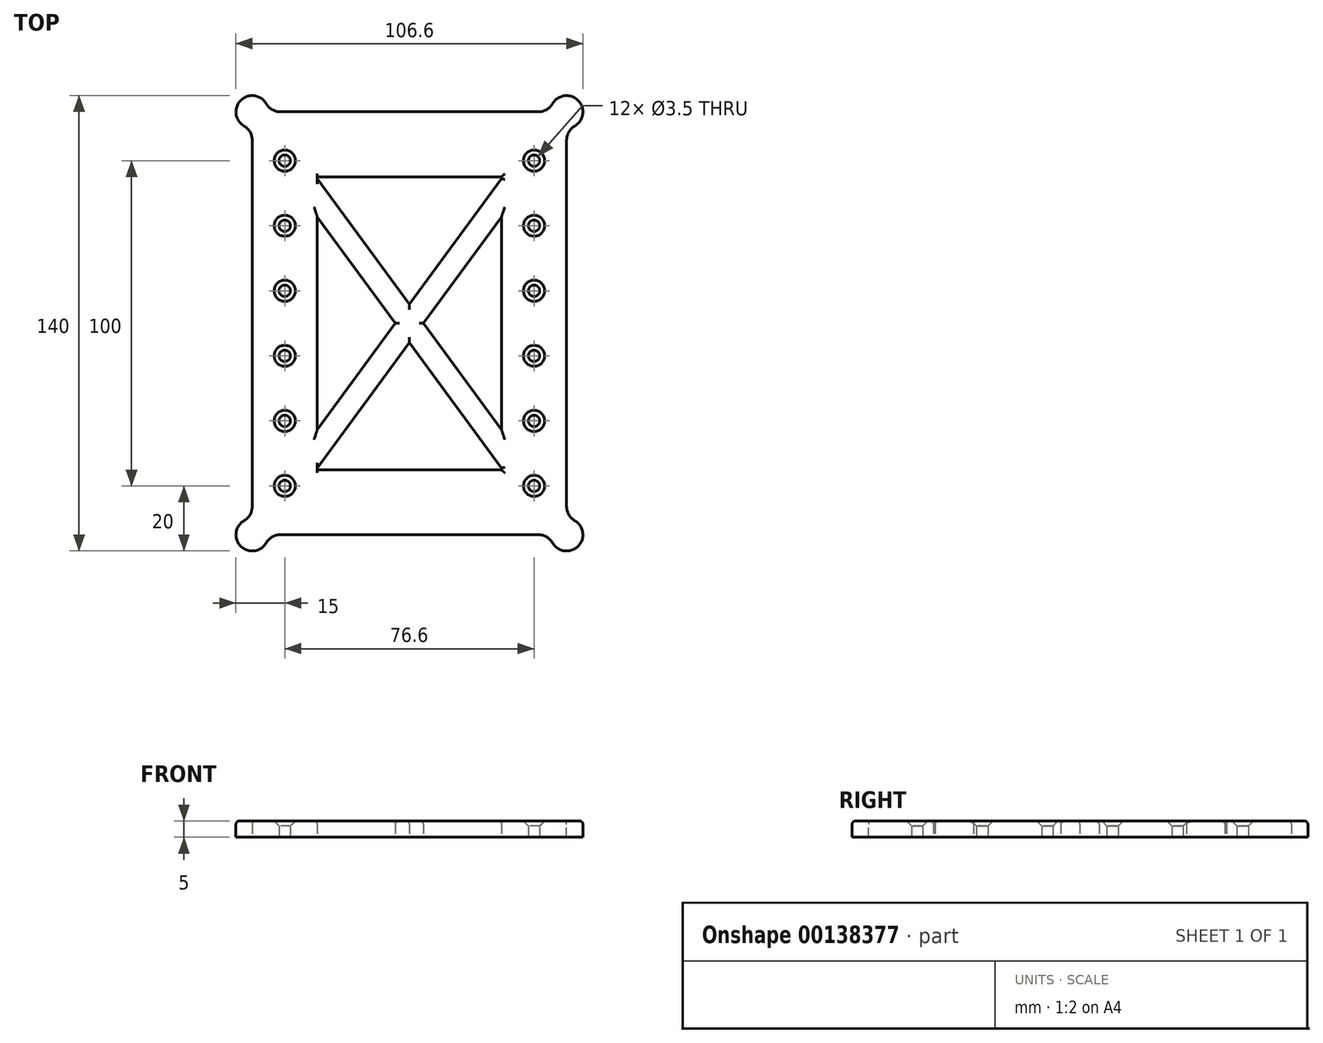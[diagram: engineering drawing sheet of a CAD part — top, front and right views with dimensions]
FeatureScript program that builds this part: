
annotation { "Feature Type Name" : "Feature", "Feature Type Description" : "" }
export const myFeature = defineFeature(function(context is Context, id is Id, definition is map)
    precondition{}
    {
        {
            var Q0;
            Q0=qCreatedBy(makeId("Top.planeOp"),FACE);
            var sketch = newSketch(context, id + "F0", { "sketchPlane" : qUnion([Q0])});
            skLineSegment(sketch, "E0.bottom", {"start": v(5, 0) * mm, "end": v(91.6, 0) * mm});
            skLineSegment(sketch, "E0.top", {"start": v(5, 130) * mm, "end": v(91.6, 130) * mm});
            skLineSegment(sketch, "E0.left", {"start": v(0, 5) * mm, "end": v(0, 125) * mm});
            skLineSegment(sketch, "E0.right", {"start": v(96.6, 5) * mm, "end": v(96.6, 125) * mm});
            skCircle(sketch, "E1", {"center": v(10, 15) * mm, "radius": 1.75 * mm});
            skCircle(sketch, "E2.0.1.0", {"center": v(10, 35) * mm, "radius": 1.75 * mm});
            skCircle(sketch, "E2.0.2.0", {"center": v(10, 55) * mm, "radius": 1.75 * mm});
            skCircle(sketch, "E2.0.3.0", {"center": v(10, 75) * mm, "radius": 1.75 * mm});
            skCircle(sketch, "E2.0.4.0", {"center": v(10, 95) * mm, "radius": 1.75 * mm});
            skCircle(sketch, "E2.0.5.0", {"center": v(10, 115) * mm, "radius": 1.75 * mm});
            skCircle(sketch, "E2.1.0.0", {"center": v(86.6, 15) * mm, "radius": 1.75 * mm});
            skCircle(sketch, "E2.1.1.0", {"center": v(86.6, 35) * mm, "radius": 1.75 * mm});
            skCircle(sketch, "E2.1.2.0", {"center": v(86.6, 55) * mm, "radius": 1.75 * mm});
            skCircle(sketch, "E2.1.3.0", {"center": v(86.6, 75) * mm, "radius": 1.75 * mm});
            skCircle(sketch, "E2.1.4.0", {"center": v(86.6, 95) * mm, "radius": 1.75 * mm});
            skCircle(sketch, "E2.1.5.0", {"center": v(86.6, 115) * mm, "radius": 1.75 * mm});
            skLineSegment(sketch, "E2.direction1", {"start": v(10, 15) * mm, "end": v(86.6, 15) * mm, "construction": true});
            skLineSegment(sketch, "E2.direction2", {"start": v(10, 15) * mm, "end": v(10, 35) * mm, "construction": true});
            skArc(sketch, "E3", {"start": v(0, 5) * mm, "mid": v(-3.54, -3.54) * mm, "end": v(5, 0) * mm});
            skArc(sketch, "E4", {"start": v(91.6, 0) * mm, "mid": v(100.14, -3.54) * mm, "end": v(96.6, 5) * mm});
            skArc(sketch, "E5", {"start": v(96.6, 125) * mm, "mid": v(100.14, 133.54) * mm, "end": v(91.6, 130) * mm});
            skArc(sketch, "E6", {"start": v(5, 130) * mm, "mid": v(-3.54, 133.54) * mm, "end": v(0, 125) * mm});
            skLineSegment(sketch, "E7.0", {"start": v(20, 20) * mm, "end": v(20, 20.47) * mm});
            skLineSegment(sketch, "E7.2", {"start": v(76.6, 20) * mm, "end": v(76.6, 20.47) * mm});
            skLineSegment(sketch, "E7.3", {"start": v(20, 110) * mm, "end": v(45.8, 110) * mm});
            skLineSegment(sketch, "E8.trimOffspring", {"start": v(76.6, 67.5) * mm, "end": v(76.6, 97.7) * mm});
            skLineSegment(sketch, "E9.trimOffspring", {"start": v(20, 67.5) * mm, "end": v(20, 97.7) * mm});
            skLineSegment(sketch, "E10.trimOffspring", {"start": v(50.8, 110) * mm, "end": v(76.6, 110) * mm});
            skLineSegment(sketch, "E11", {"start": v(20, 97.7) * mm, "end": v(42.14, 67.5) * mm});
            skLineSegment(sketch, "E12", {"start": v(76.6, 32.3) * mm, "end": v(54.46, 62.5) * mm});
            skLineSegment(sketch, "E13", {"start": v(76.6, 109.53) * mm, "end": v(50.8, 74.32) * mm});
            skLineSegment(sketch, "E14", {"start": v(20, 20.47) * mm, "end": v(45.8, 55.68) * mm});
            skLineSegment(sketch, "E15.trimOffspring", {"start": v(20, 109.53) * mm, "end": v(20, 110) * mm});
            skLineSegment(sketch, "E16.trimOffspring", {"start": v(20, 32.3) * mm, "end": v(20, 62.5) * mm});
            skLineSegment(sketch, "E17.trimOffspring", {"start": v(76.6, 32.3) * mm, "end": v(76.6, 62.5) * mm});
            skLineSegment(sketch, "E18.trimOffspring", {"start": v(76.6, 109.53) * mm, "end": v(76.6, 110) * mm});
            skLineSegment(sketch, "E19.trimOffspring", {"start": v(42.14, 62.5) * mm, "end": v(20, 32.3) * mm});
            skLineSegment(sketch, "E20.trimOffspring", {"start": v(45.8, 74.32) * mm, "end": v(20, 109.53) * mm});
            skLineSegment(sketch, "E21.trimOffspring", {"start": v(54.46, 67.5) * mm, "end": v(76.6, 97.7) * mm});
            skLineSegment(sketch, "E22.trimOffspring", {"start": v(50.8, 55.68) * mm, "end": v(76.6, 20.47) * mm});
            skLineSegment(sketch, "E23", {"start": v(20, 20.47) * mm, "end": v(48.3, 59.09) * mm});
            skLineSegment(sketch, "E24", {"start": v(76.6, 109.53) * mm, "end": v(48.3, 70.91) * mm});
            skLineSegment(sketch, "E25", {"start": v(20, 109.53) * mm, "end": v(48.3, 70.91) * mm});
            skLineSegment(sketch, "E26", {"start": v(20, 110) * mm, "end": v(20, 109.53) * mm});
            skLineSegment(sketch, "E27", {"start": v(20, 110) * mm, "end": v(76.6, 110) * mm});
            skLineSegment(sketch, "E28.trimOffspring", {"start": v(52.63, 65) * mm, "end": v(76.6, 32.3) * mm});
            skLineSegment(sketch, "E29.trimOffspring", {"start": v(43.97, 65) * mm, "end": v(20, 32.3) * mm});
            skLineSegment(sketch, "E30.trimOffspring", {"start": v(43.97, 65) * mm, "end": v(20, 97.7) * mm});
            skLineSegment(sketch, "E31.trimOffspring", {"start": v(52.63, 65) * mm, "end": v(76.6, 97.7) * mm});
            skLineSegment(sketch, "E32.trimOffspring", {"start": v(20, 20.47) * mm, "end": v(20, 20) * mm});
            skLineSegment(sketch, "E33.trimOffspring", {"start": v(76.6, 32.3) * mm, "end": v(76.6, 97.7) * mm});
            skLineSegment(sketch, "E34.trimOffspring", {"start": v(20, 97.7) * mm, "end": v(20, 32.3) * mm});
            skLineSegment(sketch, "E35", {"start": v(20, 20) * mm, "end": v(76.6, 20) * mm});
            skLineSegment(sketch, "E36.trimOffspring", {"start": v(76.6, 20.47) * mm, "end": v(48.3, 59.09) * mm});
            skSolve(sketch);
        }
        {
            var Q0;
            Q0=makeQuery(id+"F0.imprint","IMPRINT",FACE,{"disambiguationData":[TD([[makeQuery(id+"F0.imprint","IMPRINT",EDGE,{"derivedFrom":sQuery(id+"F0.wireOp",EDGE,"E0.bottom")}),1.0]])]});
            extrude(context, id + "F1", {"entities" : qUnion([Q0]), "depth" : 5 * mm});
        }
        {
            var Q0;
            Q0=makeQuery(id+"F1.opExtrude","CAP_EDGE",EDGE,{"disambiguationData":[OSD([sQuery(id+"F0.wireOp",EDGE,"E1")])],"isStart":false});
            var Q1;
            Q1=makeQuery(id+"F1.opExtrude","CAP_EDGE",EDGE,{"disambiguationData":[OSD([sQuery(id+"F0.wireOp",EDGE,"E2.0.1.0")])],"isStart":false});
            var Q2;
            Q2=makeQuery(id+"F1.opExtrude","CAP_EDGE",EDGE,{"disambiguationData":[OSD([sQuery(id+"F0.wireOp",EDGE,"E2.0.2.0")])],"isStart":false});
            var Q3;
            Q3=makeQuery(id+"F1.opExtrude","CAP_EDGE",EDGE,{"disambiguationData":[OSD([sQuery(id+"F0.wireOp",EDGE,"E2.0.3.0")])],"isStart":false});
            var Q4;
            Q4=makeQuery(id+"F1.opExtrude","CAP_EDGE",EDGE,{"disambiguationData":[OSD([sQuery(id+"F0.wireOp",EDGE,"E2.0.4.0")])],"isStart":false});
            var Q5;
            Q5=makeQuery(id+"F1.opExtrude","CAP_EDGE",EDGE,{"disambiguationData":[OSD([sQuery(id+"F0.wireOp",EDGE,"E2.0.5.0")])],"isStart":false});
            var Q6;
            Q6=makeQuery(id+"F1.opExtrude","CAP_EDGE",EDGE,{"disambiguationData":[OSD([sQuery(id+"F0.wireOp",EDGE,"E2.1.5.0")])],"isStart":false});
            var Q7;
            Q7=makeQuery(id+"F1.opExtrude","CAP_EDGE",EDGE,{"disambiguationData":[OSD([sQuery(id+"F0.wireOp",EDGE,"E2.1.4.0")])],"isStart":false});
            var Q8;
            Q8=makeQuery(id+"F1.opExtrude","CAP_EDGE",EDGE,{"disambiguationData":[OSD([sQuery(id+"F0.wireOp",EDGE,"E2.1.3.0")])],"isStart":false});
            var Q9;
            Q9=makeQuery(id+"F1.opExtrude","CAP_EDGE",EDGE,{"disambiguationData":[OSD([sQuery(id+"F0.wireOp",EDGE,"E2.1.2.0")])],"isStart":false});
            var Q10;
            Q10=makeQuery(id+"F1.opExtrude","CAP_EDGE",EDGE,{"disambiguationData":[OSD([sQuery(id+"F0.wireOp",EDGE,"E2.1.1.0")])],"isStart":false});
            var Q11;
            Q11=makeQuery(id+"F1.opExtrude","CAP_EDGE",EDGE,{"disambiguationData":[OSD([sQuery(id+"F0.wireOp",EDGE,"E2.1.0.0")])],"isStart":false});
            chamfer(context, id + "F2", {"entities" : qUnion([Q0, Q1, Q2, Q3, Q4, Q5, Q6, Q7, Q8, Q9, Q10, Q11]), "width" : 1.5 * mm, "tangentPropagation" : true});
        }
        {
            var Q0;
            Q0=makeQuery(id+"F1.opExtrude","SWEPT_EDGE",EDGE,{"disambiguationData":[OSD([sQuery(id+"F0.wireOp",EDGE,"E0.bottom"),sQuery(id+"F0.wireOp",EDGE,"E3")])]});
            var Q1;
            Q1=makeQuery(id+"F1.opExtrude","SWEPT_EDGE",EDGE,{"disambiguationData":[OSD([sQuery(id+"F0.wireOp",EDGE,"E0.bottom"),sQuery(id+"F0.wireOp",EDGE,"E4")])]});
            var Q2;
            Q2=makeQuery(id+"F1.opExtrude","SWEPT_EDGE",EDGE,{"disambiguationData":[OSD([sQuery(id+"F0.wireOp",EDGE,"E0.right"),sQuery(id+"F0.wireOp",EDGE,"E4")])]});
            var Q3;
            Q3=makeQuery(id+"F1.opExtrude","SWEPT_EDGE",EDGE,{"disambiguationData":[OSD([sQuery(id+"F0.wireOp",EDGE,"E0.right"),sQuery(id+"F0.wireOp",EDGE,"E5")])]});
            var Q4;
            Q4=makeQuery(id+"F1.opExtrude","SWEPT_EDGE",EDGE,{"disambiguationData":[OSD([sQuery(id+"F0.wireOp",EDGE,"E0.top"),sQuery(id+"F0.wireOp",EDGE,"E5")])]});
            var Q5;
            Q5=makeQuery(id+"F1.opExtrude","SWEPT_EDGE",EDGE,{"disambiguationData":[OSD([sQuery(id+"F0.wireOp",EDGE,"E0.top"),sQuery(id+"F0.wireOp",EDGE,"E6")])]});
            var Q6;
            Q6=makeQuery(id+"F1.opExtrude","SWEPT_EDGE",EDGE,{"disambiguationData":[OSD([sQuery(id+"F0.wireOp",EDGE,"E0.left"),sQuery(id+"F0.wireOp",EDGE,"E6")])]});
            var Q7;
            Q7=makeQuery(id+"F1.opExtrude","SWEPT_EDGE",EDGE,{"disambiguationData":[OSD([sQuery(id+"F0.wireOp",EDGE,"E0.left"),sQuery(id+"F0.wireOp",EDGE,"E3")])]});
            fillet(context, id + "F3", {"entities" : qUnion([Q0, Q1, Q2, Q3, Q4, Q5, Q6, Q7]), "radius" : 5 * mm, "tangentPropagation" : true, "allowEdgeOverflow" : false});
        }
        {
            var Q0;
            Q0=makeQuery(id+"F1.opExtrude","CAP_EDGE",EDGE,{"disambiguationData":[OSD([sQuery(id+"F0.wireOp",EDGE,"E0.bottom")])],"isStart":false});
            var Q1;
            Q1=makeQuery(id+"F1.opExtrude","CAP_EDGE",EDGE,{"disambiguationData":[OSD([sQuery(id+"F0.wireOp",EDGE,"E4")])],"isStart":false});
            var Q2;
            {var subQ0=sQuery(id+"F0.wireOp",EDGE,"E4");var subQ1=sQuery(id+"F0.wireOp",EDGE,"E0.bottom");Q2=makeQuery(id+"F3.opFillet","BLEND_EDGE",EDGE,{"blendedFrom":[makeQuery(id+"F1.opExtrude","SWEPT_EDGE",EDGE,{"disambiguationData":[OSD([subQ1,subQ0])]}),makeQuery(id+"F1.opExtrude","CAP_FACE",FACE,{"disambiguationData":[OSD([subQ1,sQuery(id+"F0.wireOp",EDGE,"E0.top"),sQuery(id+"F0.wireOp",EDGE,"E0.left"),sQuery(id+"F0.wireOp",EDGE,"E0.right"),sQuery(id+"F0.wireOp",EDGE,"E1"),sQuery(id+"F0.wireOp",EDGE,"E2.0.1.0"),sQuery(id+"F0.wireOp",EDGE,"E2.0.2.0"),sQuery(id+"F0.wireOp",EDGE,"E2.0.3.0"),sQuery(id+"F0.wireOp",EDGE,"E2.0.4.0"),sQuery(id+"F0.wireOp",EDGE,"E2.0.5.0"),sQuery(id+"F0.wireOp",EDGE,"E2.1.0.0"),sQuery(id+"F0.wireOp",EDGE,"E2.1.1.0"),sQuery(id+"F0.wireOp",EDGE,"E2.1.2.0"),sQuery(id+"F0.wireOp",EDGE,"E2.1.3.0"),sQuery(id+"F0.wireOp",EDGE,"E2.1.4.0"),sQuery(id+"F0.wireOp",EDGE,"E2.1.5.0"),sQuery(id+"F0.wireOp",EDGE,"E3"),subQ0,sQuery(id+"F0.wireOp",EDGE,"E5"),sQuery(id+"F0.wireOp",EDGE,"E6"),sQuery(id+"F0.wireOp",EDGE,"E23"),sQuery(id+"F0.wireOp",EDGE,"E24"),sQuery(id+"F0.wireOp",EDGE,"E25"),sQuery(id+"F0.wireOp",EDGE,"E7.2"),sQuery(id+"F0.wireOp",EDGE,"E26"),sQuery(id+"F0.wireOp",EDGE,"E27"),sQuery(id+"F0.wireOp",EDGE,"E28.trimOffspring"),sQuery(id+"F0.wireOp",EDGE,"E29.trimOffspring"),sQuery(id+"F0.wireOp",EDGE,"E30.trimOffspring"),sQuery(id+"F0.wireOp",EDGE,"E31.trimOffspring"),sQuery(id+"F0.wireOp",EDGE,"E32.trimOffspring"),sQuery(id+"F0.wireOp",EDGE,"E33.trimOffspring"),sQuery(id+"F0.wireOp",EDGE,"E34.trimOffspring"),sQuery(id+"F0.wireOp",EDGE,"E18.trimOffspring"),sQuery(id+"F0.wireOp",EDGE,"E35"),sQuery(id+"F0.wireOp",EDGE,"E36.trimOffspring")])],"isStart":false})],"blendedInto":[makeQuery(id+"F1.opExtrude","CAP_FACE",FACE,{"disambiguationData":[OSD([subQ1,sQuery(id+"F0.wireOp",EDGE,"E0.top"),sQuery(id+"F0.wireOp",EDGE,"E0.left"),sQuery(id+"F0.wireOp",EDGE,"E0.right"),sQuery(id+"F0.wireOp",EDGE,"E1"),sQuery(id+"F0.wireOp",EDGE,"E2.0.1.0"),sQuery(id+"F0.wireOp",EDGE,"E2.0.2.0"),sQuery(id+"F0.wireOp",EDGE,"E2.0.3.0"),sQuery(id+"F0.wireOp",EDGE,"E2.0.4.0"),sQuery(id+"F0.wireOp",EDGE,"E2.0.5.0"),sQuery(id+"F0.wireOp",EDGE,"E2.1.0.0"),sQuery(id+"F0.wireOp",EDGE,"E2.1.1.0"),sQuery(id+"F0.wireOp",EDGE,"E2.1.2.0"),sQuery(id+"F0.wireOp",EDGE,"E2.1.3.0"),sQuery(id+"F0.wireOp",EDGE,"E2.1.4.0"),sQuery(id+"F0.wireOp",EDGE,"E2.1.5.0"),sQuery(id+"F0.wireOp",EDGE,"E3"),subQ0,sQuery(id+"F0.wireOp",EDGE,"E5"),sQuery(id+"F0.wireOp",EDGE,"E6"),sQuery(id+"F0.wireOp",EDGE,"E23"),sQuery(id+"F0.wireOp",EDGE,"E24"),sQuery(id+"F0.wireOp",EDGE,"E25"),sQuery(id+"F0.wireOp",EDGE,"E7.2"),sQuery(id+"F0.wireOp",EDGE,"E26"),sQuery(id+"F0.wireOp",EDGE,"E27"),sQuery(id+"F0.wireOp",EDGE,"E28.trimOffspring"),sQuery(id+"F0.wireOp",EDGE,"E29.trimOffspring"),sQuery(id+"F0.wireOp",EDGE,"E30.trimOffspring"),sQuery(id+"F0.wireOp",EDGE,"E31.trimOffspring"),sQuery(id+"F0.wireOp",EDGE,"E32.trimOffspring"),sQuery(id+"F0.wireOp",EDGE,"E33.trimOffspring"),sQuery(id+"F0.wireOp",EDGE,"E34.trimOffspring"),sQuery(id+"F0.wireOp",EDGE,"E18.trimOffspring"),sQuery(id+"F0.wireOp",EDGE,"E35"),sQuery(id+"F0.wireOp",EDGE,"E36.trimOffspring")])],"isStart":false})]});}
            var Q3;
            {var subQ0=sQuery(id+"F0.wireOp",EDGE,"E4");var subQ1=sQuery(id+"F0.wireOp",EDGE,"E0.right");Q3=makeQuery(id+"F3.opFillet","BLEND_EDGE",EDGE,{"blendedFrom":[makeQuery(id+"F1.opExtrude","SWEPT_EDGE",EDGE,{"disambiguationData":[OSD([subQ1,subQ0])]}),makeQuery(id+"F1.opExtrude","CAP_FACE",FACE,{"disambiguationData":[OSD([sQuery(id+"F0.wireOp",EDGE,"E0.bottom"),sQuery(id+"F0.wireOp",EDGE,"E0.top"),sQuery(id+"F0.wireOp",EDGE,"E0.left"),subQ1,sQuery(id+"F0.wireOp",EDGE,"E1"),sQuery(id+"F0.wireOp",EDGE,"E2.0.1.0"),sQuery(id+"F0.wireOp",EDGE,"E2.0.2.0"),sQuery(id+"F0.wireOp",EDGE,"E2.0.3.0"),sQuery(id+"F0.wireOp",EDGE,"E2.0.4.0"),sQuery(id+"F0.wireOp",EDGE,"E2.0.5.0"),sQuery(id+"F0.wireOp",EDGE,"E2.1.0.0"),sQuery(id+"F0.wireOp",EDGE,"E2.1.1.0"),sQuery(id+"F0.wireOp",EDGE,"E2.1.2.0"),sQuery(id+"F0.wireOp",EDGE,"E2.1.3.0"),sQuery(id+"F0.wireOp",EDGE,"E2.1.4.0"),sQuery(id+"F0.wireOp",EDGE,"E2.1.5.0"),sQuery(id+"F0.wireOp",EDGE,"E3"),subQ0,sQuery(id+"F0.wireOp",EDGE,"E5"),sQuery(id+"F0.wireOp",EDGE,"E6"),sQuery(id+"F0.wireOp",EDGE,"E23"),sQuery(id+"F0.wireOp",EDGE,"E24"),sQuery(id+"F0.wireOp",EDGE,"E25"),sQuery(id+"F0.wireOp",EDGE,"E7.2"),sQuery(id+"F0.wireOp",EDGE,"E26"),sQuery(id+"F0.wireOp",EDGE,"E27"),sQuery(id+"F0.wireOp",EDGE,"E28.trimOffspring"),sQuery(id+"F0.wireOp",EDGE,"E29.trimOffspring"),sQuery(id+"F0.wireOp",EDGE,"E30.trimOffspring"),sQuery(id+"F0.wireOp",EDGE,"E31.trimOffspring"),sQuery(id+"F0.wireOp",EDGE,"E32.trimOffspring"),sQuery(id+"F0.wireOp",EDGE,"E33.trimOffspring"),sQuery(id+"F0.wireOp",EDGE,"E34.trimOffspring"),sQuery(id+"F0.wireOp",EDGE,"E18.trimOffspring"),sQuery(id+"F0.wireOp",EDGE,"E35"),sQuery(id+"F0.wireOp",EDGE,"E36.trimOffspring")])],"isStart":false})],"blendedInto":[makeQuery(id+"F1.opExtrude","CAP_FACE",FACE,{"disambiguationData":[OSD([sQuery(id+"F0.wireOp",EDGE,"E0.bottom"),sQuery(id+"F0.wireOp",EDGE,"E0.top"),sQuery(id+"F0.wireOp",EDGE,"E0.left"),subQ1,sQuery(id+"F0.wireOp",EDGE,"E1"),sQuery(id+"F0.wireOp",EDGE,"E2.0.1.0"),sQuery(id+"F0.wireOp",EDGE,"E2.0.2.0"),sQuery(id+"F0.wireOp",EDGE,"E2.0.3.0"),sQuery(id+"F0.wireOp",EDGE,"E2.0.4.0"),sQuery(id+"F0.wireOp",EDGE,"E2.0.5.0"),sQuery(id+"F0.wireOp",EDGE,"E2.1.0.0"),sQuery(id+"F0.wireOp",EDGE,"E2.1.1.0"),sQuery(id+"F0.wireOp",EDGE,"E2.1.2.0"),sQuery(id+"F0.wireOp",EDGE,"E2.1.3.0"),sQuery(id+"F0.wireOp",EDGE,"E2.1.4.0"),sQuery(id+"F0.wireOp",EDGE,"E2.1.5.0"),sQuery(id+"F0.wireOp",EDGE,"E3"),subQ0,sQuery(id+"F0.wireOp",EDGE,"E5"),sQuery(id+"F0.wireOp",EDGE,"E6"),sQuery(id+"F0.wireOp",EDGE,"E23"),sQuery(id+"F0.wireOp",EDGE,"E24"),sQuery(id+"F0.wireOp",EDGE,"E25"),sQuery(id+"F0.wireOp",EDGE,"E7.2"),sQuery(id+"F0.wireOp",EDGE,"E26"),sQuery(id+"F0.wireOp",EDGE,"E27"),sQuery(id+"F0.wireOp",EDGE,"E28.trimOffspring"),sQuery(id+"F0.wireOp",EDGE,"E29.trimOffspring"),sQuery(id+"F0.wireOp",EDGE,"E30.trimOffspring"),sQuery(id+"F0.wireOp",EDGE,"E31.trimOffspring"),sQuery(id+"F0.wireOp",EDGE,"E32.trimOffspring"),sQuery(id+"F0.wireOp",EDGE,"E33.trimOffspring"),sQuery(id+"F0.wireOp",EDGE,"E34.trimOffspring"),sQuery(id+"F0.wireOp",EDGE,"E18.trimOffspring"),sQuery(id+"F0.wireOp",EDGE,"E35"),sQuery(id+"F0.wireOp",EDGE,"E36.trimOffspring")])],"isStart":false})]});}
            var Q4;
            Q4=makeQuery(id+"F1.opExtrude","CAP_EDGE",EDGE,{"disambiguationData":[OSD([sQuery(id+"F0.wireOp",EDGE,"E0.right")])],"isStart":false});
            var Q5;
            {var subQ0=sQuery(id+"F0.wireOp",EDGE,"E5");var subQ1=sQuery(id+"F0.wireOp",EDGE,"E0.right");Q5=makeQuery(id+"F3.opFillet","BLEND_EDGE",EDGE,{"blendedFrom":[makeQuery(id+"F1.opExtrude","SWEPT_EDGE",EDGE,{"disambiguationData":[OSD([subQ1,subQ0])]}),makeQuery(id+"F1.opExtrude","CAP_FACE",FACE,{"disambiguationData":[OSD([sQuery(id+"F0.wireOp",EDGE,"E0.bottom"),sQuery(id+"F0.wireOp",EDGE,"E0.top"),sQuery(id+"F0.wireOp",EDGE,"E0.left"),subQ1,sQuery(id+"F0.wireOp",EDGE,"E1"),sQuery(id+"F0.wireOp",EDGE,"E2.0.1.0"),sQuery(id+"F0.wireOp",EDGE,"E2.0.2.0"),sQuery(id+"F0.wireOp",EDGE,"E2.0.3.0"),sQuery(id+"F0.wireOp",EDGE,"E2.0.4.0"),sQuery(id+"F0.wireOp",EDGE,"E2.0.5.0"),sQuery(id+"F0.wireOp",EDGE,"E2.1.0.0"),sQuery(id+"F0.wireOp",EDGE,"E2.1.1.0"),sQuery(id+"F0.wireOp",EDGE,"E2.1.2.0"),sQuery(id+"F0.wireOp",EDGE,"E2.1.3.0"),sQuery(id+"F0.wireOp",EDGE,"E2.1.4.0"),sQuery(id+"F0.wireOp",EDGE,"E2.1.5.0"),sQuery(id+"F0.wireOp",EDGE,"E3"),sQuery(id+"F0.wireOp",EDGE,"E4"),subQ0,sQuery(id+"F0.wireOp",EDGE,"E6"),sQuery(id+"F0.wireOp",EDGE,"E23"),sQuery(id+"F0.wireOp",EDGE,"E24"),sQuery(id+"F0.wireOp",EDGE,"E25"),sQuery(id+"F0.wireOp",EDGE,"E7.2"),sQuery(id+"F0.wireOp",EDGE,"E26"),sQuery(id+"F0.wireOp",EDGE,"E27"),sQuery(id+"F0.wireOp",EDGE,"E28.trimOffspring"),sQuery(id+"F0.wireOp",EDGE,"E29.trimOffspring"),sQuery(id+"F0.wireOp",EDGE,"E30.trimOffspring"),sQuery(id+"F0.wireOp",EDGE,"E31.trimOffspring"),sQuery(id+"F0.wireOp",EDGE,"E32.trimOffspring"),sQuery(id+"F0.wireOp",EDGE,"E33.trimOffspring"),sQuery(id+"F0.wireOp",EDGE,"E34.trimOffspring"),sQuery(id+"F0.wireOp",EDGE,"E18.trimOffspring"),sQuery(id+"F0.wireOp",EDGE,"E35"),sQuery(id+"F0.wireOp",EDGE,"E36.trimOffspring")])],"isStart":false})],"blendedInto":[makeQuery(id+"F1.opExtrude","CAP_FACE",FACE,{"disambiguationData":[OSD([sQuery(id+"F0.wireOp",EDGE,"E0.bottom"),sQuery(id+"F0.wireOp",EDGE,"E0.top"),sQuery(id+"F0.wireOp",EDGE,"E0.left"),subQ1,sQuery(id+"F0.wireOp",EDGE,"E1"),sQuery(id+"F0.wireOp",EDGE,"E2.0.1.0"),sQuery(id+"F0.wireOp",EDGE,"E2.0.2.0"),sQuery(id+"F0.wireOp",EDGE,"E2.0.3.0"),sQuery(id+"F0.wireOp",EDGE,"E2.0.4.0"),sQuery(id+"F0.wireOp",EDGE,"E2.0.5.0"),sQuery(id+"F0.wireOp",EDGE,"E2.1.0.0"),sQuery(id+"F0.wireOp",EDGE,"E2.1.1.0"),sQuery(id+"F0.wireOp",EDGE,"E2.1.2.0"),sQuery(id+"F0.wireOp",EDGE,"E2.1.3.0"),sQuery(id+"F0.wireOp",EDGE,"E2.1.4.0"),sQuery(id+"F0.wireOp",EDGE,"E2.1.5.0"),sQuery(id+"F0.wireOp",EDGE,"E3"),sQuery(id+"F0.wireOp",EDGE,"E4"),subQ0,sQuery(id+"F0.wireOp",EDGE,"E6"),sQuery(id+"F0.wireOp",EDGE,"E23"),sQuery(id+"F0.wireOp",EDGE,"E24"),sQuery(id+"F0.wireOp",EDGE,"E25"),sQuery(id+"F0.wireOp",EDGE,"E7.2"),sQuery(id+"F0.wireOp",EDGE,"E26"),sQuery(id+"F0.wireOp",EDGE,"E27"),sQuery(id+"F0.wireOp",EDGE,"E28.trimOffspring"),sQuery(id+"F0.wireOp",EDGE,"E29.trimOffspring"),sQuery(id+"F0.wireOp",EDGE,"E30.trimOffspring"),sQuery(id+"F0.wireOp",EDGE,"E31.trimOffspring"),sQuery(id+"F0.wireOp",EDGE,"E32.trimOffspring"),sQuery(id+"F0.wireOp",EDGE,"E33.trimOffspring"),sQuery(id+"F0.wireOp",EDGE,"E34.trimOffspring"),sQuery(id+"F0.wireOp",EDGE,"E18.trimOffspring"),sQuery(id+"F0.wireOp",EDGE,"E35"),sQuery(id+"F0.wireOp",EDGE,"E36.trimOffspring")])],"isStart":false})]});}
            var Q6;
            Q6=makeQuery(id+"F1.opExtrude","CAP_EDGE",EDGE,{"disambiguationData":[OSD([sQuery(id+"F0.wireOp",EDGE,"E5")])],"isStart":false});
            var Q7;
            {var subQ0=sQuery(id+"F0.wireOp",EDGE,"E5");var subQ1=sQuery(id+"F0.wireOp",EDGE,"E0.top");Q7=makeQuery(id+"F3.opFillet","BLEND_EDGE",EDGE,{"blendedFrom":[makeQuery(id+"F1.opExtrude","SWEPT_EDGE",EDGE,{"disambiguationData":[OSD([subQ1,subQ0])]}),makeQuery(id+"F1.opExtrude","CAP_FACE",FACE,{"disambiguationData":[OSD([sQuery(id+"F0.wireOp",EDGE,"E0.bottom"),subQ1,sQuery(id+"F0.wireOp",EDGE,"E0.left"),sQuery(id+"F0.wireOp",EDGE,"E0.right"),sQuery(id+"F0.wireOp",EDGE,"E1"),sQuery(id+"F0.wireOp",EDGE,"E2.0.1.0"),sQuery(id+"F0.wireOp",EDGE,"E2.0.2.0"),sQuery(id+"F0.wireOp",EDGE,"E2.0.3.0"),sQuery(id+"F0.wireOp",EDGE,"E2.0.4.0"),sQuery(id+"F0.wireOp",EDGE,"E2.0.5.0"),sQuery(id+"F0.wireOp",EDGE,"E2.1.0.0"),sQuery(id+"F0.wireOp",EDGE,"E2.1.1.0"),sQuery(id+"F0.wireOp",EDGE,"E2.1.2.0"),sQuery(id+"F0.wireOp",EDGE,"E2.1.3.0"),sQuery(id+"F0.wireOp",EDGE,"E2.1.4.0"),sQuery(id+"F0.wireOp",EDGE,"E2.1.5.0"),sQuery(id+"F0.wireOp",EDGE,"E3"),sQuery(id+"F0.wireOp",EDGE,"E4"),subQ0,sQuery(id+"F0.wireOp",EDGE,"E6"),sQuery(id+"F0.wireOp",EDGE,"E23"),sQuery(id+"F0.wireOp",EDGE,"E24"),sQuery(id+"F0.wireOp",EDGE,"E25"),sQuery(id+"F0.wireOp",EDGE,"E7.2"),sQuery(id+"F0.wireOp",EDGE,"E26"),sQuery(id+"F0.wireOp",EDGE,"E27"),sQuery(id+"F0.wireOp",EDGE,"E28.trimOffspring"),sQuery(id+"F0.wireOp",EDGE,"E29.trimOffspring"),sQuery(id+"F0.wireOp",EDGE,"E30.trimOffspring"),sQuery(id+"F0.wireOp",EDGE,"E31.trimOffspring"),sQuery(id+"F0.wireOp",EDGE,"E32.trimOffspring"),sQuery(id+"F0.wireOp",EDGE,"E33.trimOffspring"),sQuery(id+"F0.wireOp",EDGE,"E34.trimOffspring"),sQuery(id+"F0.wireOp",EDGE,"E18.trimOffspring"),sQuery(id+"F0.wireOp",EDGE,"E35"),sQuery(id+"F0.wireOp",EDGE,"E36.trimOffspring")])],"isStart":false})],"blendedInto":[makeQuery(id+"F1.opExtrude","CAP_FACE",FACE,{"disambiguationData":[OSD([sQuery(id+"F0.wireOp",EDGE,"E0.bottom"),subQ1,sQuery(id+"F0.wireOp",EDGE,"E0.left"),sQuery(id+"F0.wireOp",EDGE,"E0.right"),sQuery(id+"F0.wireOp",EDGE,"E1"),sQuery(id+"F0.wireOp",EDGE,"E2.0.1.0"),sQuery(id+"F0.wireOp",EDGE,"E2.0.2.0"),sQuery(id+"F0.wireOp",EDGE,"E2.0.3.0"),sQuery(id+"F0.wireOp",EDGE,"E2.0.4.0"),sQuery(id+"F0.wireOp",EDGE,"E2.0.5.0"),sQuery(id+"F0.wireOp",EDGE,"E2.1.0.0"),sQuery(id+"F0.wireOp",EDGE,"E2.1.1.0"),sQuery(id+"F0.wireOp",EDGE,"E2.1.2.0"),sQuery(id+"F0.wireOp",EDGE,"E2.1.3.0"),sQuery(id+"F0.wireOp",EDGE,"E2.1.4.0"),sQuery(id+"F0.wireOp",EDGE,"E2.1.5.0"),sQuery(id+"F0.wireOp",EDGE,"E3"),sQuery(id+"F0.wireOp",EDGE,"E4"),subQ0,sQuery(id+"F0.wireOp",EDGE,"E6"),sQuery(id+"F0.wireOp",EDGE,"E23"),sQuery(id+"F0.wireOp",EDGE,"E24"),sQuery(id+"F0.wireOp",EDGE,"E25"),sQuery(id+"F0.wireOp",EDGE,"E7.2"),sQuery(id+"F0.wireOp",EDGE,"E26"),sQuery(id+"F0.wireOp",EDGE,"E27"),sQuery(id+"F0.wireOp",EDGE,"E28.trimOffspring"),sQuery(id+"F0.wireOp",EDGE,"E29.trimOffspring"),sQuery(id+"F0.wireOp",EDGE,"E30.trimOffspring"),sQuery(id+"F0.wireOp",EDGE,"E31.trimOffspring"),sQuery(id+"F0.wireOp",EDGE,"E32.trimOffspring"),sQuery(id+"F0.wireOp",EDGE,"E33.trimOffspring"),sQuery(id+"F0.wireOp",EDGE,"E34.trimOffspring"),sQuery(id+"F0.wireOp",EDGE,"E18.trimOffspring"),sQuery(id+"F0.wireOp",EDGE,"E35"),sQuery(id+"F0.wireOp",EDGE,"E36.trimOffspring")])],"isStart":false})]});}
            var Q8;
            Q8=makeQuery(id+"F1.opExtrude","CAP_EDGE",EDGE,{"disambiguationData":[OSD([sQuery(id+"F0.wireOp",EDGE,"E0.top")])],"isStart":false});
            var Q9;
            {var subQ0=sQuery(id+"F0.wireOp",EDGE,"E6");var subQ1=sQuery(id+"F0.wireOp",EDGE,"E0.top");Q9=makeQuery(id+"F3.opFillet","BLEND_EDGE",EDGE,{"blendedFrom":[makeQuery(id+"F1.opExtrude","SWEPT_EDGE",EDGE,{"disambiguationData":[OSD([subQ1,subQ0])]}),makeQuery(id+"F1.opExtrude","CAP_FACE",FACE,{"disambiguationData":[OSD([sQuery(id+"F0.wireOp",EDGE,"E0.bottom"),subQ1,sQuery(id+"F0.wireOp",EDGE,"E0.left"),sQuery(id+"F0.wireOp",EDGE,"E0.right"),sQuery(id+"F0.wireOp",EDGE,"E1"),sQuery(id+"F0.wireOp",EDGE,"E2.0.1.0"),sQuery(id+"F0.wireOp",EDGE,"E2.0.2.0"),sQuery(id+"F0.wireOp",EDGE,"E2.0.3.0"),sQuery(id+"F0.wireOp",EDGE,"E2.0.4.0"),sQuery(id+"F0.wireOp",EDGE,"E2.0.5.0"),sQuery(id+"F0.wireOp",EDGE,"E2.1.0.0"),sQuery(id+"F0.wireOp",EDGE,"E2.1.1.0"),sQuery(id+"F0.wireOp",EDGE,"E2.1.2.0"),sQuery(id+"F0.wireOp",EDGE,"E2.1.3.0"),sQuery(id+"F0.wireOp",EDGE,"E2.1.4.0"),sQuery(id+"F0.wireOp",EDGE,"E2.1.5.0"),sQuery(id+"F0.wireOp",EDGE,"E3"),sQuery(id+"F0.wireOp",EDGE,"E4"),sQuery(id+"F0.wireOp",EDGE,"E5"),subQ0,sQuery(id+"F0.wireOp",EDGE,"E23"),sQuery(id+"F0.wireOp",EDGE,"E24"),sQuery(id+"F0.wireOp",EDGE,"E25"),sQuery(id+"F0.wireOp",EDGE,"E7.2"),sQuery(id+"F0.wireOp",EDGE,"E26"),sQuery(id+"F0.wireOp",EDGE,"E27"),sQuery(id+"F0.wireOp",EDGE,"E28.trimOffspring"),sQuery(id+"F0.wireOp",EDGE,"E29.trimOffspring"),sQuery(id+"F0.wireOp",EDGE,"E30.trimOffspring"),sQuery(id+"F0.wireOp",EDGE,"E31.trimOffspring"),sQuery(id+"F0.wireOp",EDGE,"E32.trimOffspring"),sQuery(id+"F0.wireOp",EDGE,"E33.trimOffspring"),sQuery(id+"F0.wireOp",EDGE,"E34.trimOffspring"),sQuery(id+"F0.wireOp",EDGE,"E18.trimOffspring"),sQuery(id+"F0.wireOp",EDGE,"E35"),sQuery(id+"F0.wireOp",EDGE,"E36.trimOffspring")])],"isStart":false})],"blendedInto":[makeQuery(id+"F1.opExtrude","CAP_FACE",FACE,{"disambiguationData":[OSD([sQuery(id+"F0.wireOp",EDGE,"E0.bottom"),subQ1,sQuery(id+"F0.wireOp",EDGE,"E0.left"),sQuery(id+"F0.wireOp",EDGE,"E0.right"),sQuery(id+"F0.wireOp",EDGE,"E1"),sQuery(id+"F0.wireOp",EDGE,"E2.0.1.0"),sQuery(id+"F0.wireOp",EDGE,"E2.0.2.0"),sQuery(id+"F0.wireOp",EDGE,"E2.0.3.0"),sQuery(id+"F0.wireOp",EDGE,"E2.0.4.0"),sQuery(id+"F0.wireOp",EDGE,"E2.0.5.0"),sQuery(id+"F0.wireOp",EDGE,"E2.1.0.0"),sQuery(id+"F0.wireOp",EDGE,"E2.1.1.0"),sQuery(id+"F0.wireOp",EDGE,"E2.1.2.0"),sQuery(id+"F0.wireOp",EDGE,"E2.1.3.0"),sQuery(id+"F0.wireOp",EDGE,"E2.1.4.0"),sQuery(id+"F0.wireOp",EDGE,"E2.1.5.0"),sQuery(id+"F0.wireOp",EDGE,"E3"),sQuery(id+"F0.wireOp",EDGE,"E4"),sQuery(id+"F0.wireOp",EDGE,"E5"),subQ0,sQuery(id+"F0.wireOp",EDGE,"E23"),sQuery(id+"F0.wireOp",EDGE,"E24"),sQuery(id+"F0.wireOp",EDGE,"E25"),sQuery(id+"F0.wireOp",EDGE,"E7.2"),sQuery(id+"F0.wireOp",EDGE,"E26"),sQuery(id+"F0.wireOp",EDGE,"E27"),sQuery(id+"F0.wireOp",EDGE,"E28.trimOffspring"),sQuery(id+"F0.wireOp",EDGE,"E29.trimOffspring"),sQuery(id+"F0.wireOp",EDGE,"E30.trimOffspring"),sQuery(id+"F0.wireOp",EDGE,"E31.trimOffspring"),sQuery(id+"F0.wireOp",EDGE,"E32.trimOffspring"),sQuery(id+"F0.wireOp",EDGE,"E33.trimOffspring"),sQuery(id+"F0.wireOp",EDGE,"E34.trimOffspring"),sQuery(id+"F0.wireOp",EDGE,"E18.trimOffspring"),sQuery(id+"F0.wireOp",EDGE,"E35"),sQuery(id+"F0.wireOp",EDGE,"E36.trimOffspring")])],"isStart":false})]});}
            var Q10;
            Q10=makeQuery(id+"F1.opExtrude","CAP_EDGE",EDGE,{"disambiguationData":[OSD([sQuery(id+"F0.wireOp",EDGE,"E6")])],"isStart":false});
            var Q11;
            {var subQ0=sQuery(id+"F0.wireOp",EDGE,"E6");var subQ1=sQuery(id+"F0.wireOp",EDGE,"E0.left");Q11=makeQuery(id+"F3.opFillet","BLEND_EDGE",EDGE,{"blendedFrom":[makeQuery(id+"F1.opExtrude","SWEPT_EDGE",EDGE,{"disambiguationData":[OSD([subQ1,subQ0])]}),makeQuery(id+"F1.opExtrude","CAP_FACE",FACE,{"disambiguationData":[OSD([sQuery(id+"F0.wireOp",EDGE,"E0.bottom"),sQuery(id+"F0.wireOp",EDGE,"E0.top"),subQ1,sQuery(id+"F0.wireOp",EDGE,"E0.right"),sQuery(id+"F0.wireOp",EDGE,"E1"),sQuery(id+"F0.wireOp",EDGE,"E2.0.1.0"),sQuery(id+"F0.wireOp",EDGE,"E2.0.2.0"),sQuery(id+"F0.wireOp",EDGE,"E2.0.3.0"),sQuery(id+"F0.wireOp",EDGE,"E2.0.4.0"),sQuery(id+"F0.wireOp",EDGE,"E2.0.5.0"),sQuery(id+"F0.wireOp",EDGE,"E2.1.0.0"),sQuery(id+"F0.wireOp",EDGE,"E2.1.1.0"),sQuery(id+"F0.wireOp",EDGE,"E2.1.2.0"),sQuery(id+"F0.wireOp",EDGE,"E2.1.3.0"),sQuery(id+"F0.wireOp",EDGE,"E2.1.4.0"),sQuery(id+"F0.wireOp",EDGE,"E2.1.5.0"),sQuery(id+"F0.wireOp",EDGE,"E3"),sQuery(id+"F0.wireOp",EDGE,"E4"),sQuery(id+"F0.wireOp",EDGE,"E5"),subQ0,sQuery(id+"F0.wireOp",EDGE,"E23"),sQuery(id+"F0.wireOp",EDGE,"E24"),sQuery(id+"F0.wireOp",EDGE,"E25"),sQuery(id+"F0.wireOp",EDGE,"E7.2"),sQuery(id+"F0.wireOp",EDGE,"E26"),sQuery(id+"F0.wireOp",EDGE,"E27"),sQuery(id+"F0.wireOp",EDGE,"E28.trimOffspring"),sQuery(id+"F0.wireOp",EDGE,"E29.trimOffspring"),sQuery(id+"F0.wireOp",EDGE,"E30.trimOffspring"),sQuery(id+"F0.wireOp",EDGE,"E31.trimOffspring"),sQuery(id+"F0.wireOp",EDGE,"E32.trimOffspring"),sQuery(id+"F0.wireOp",EDGE,"E33.trimOffspring"),sQuery(id+"F0.wireOp",EDGE,"E34.trimOffspring"),sQuery(id+"F0.wireOp",EDGE,"E18.trimOffspring"),sQuery(id+"F0.wireOp",EDGE,"E35"),sQuery(id+"F0.wireOp",EDGE,"E36.trimOffspring")])],"isStart":false})],"blendedInto":[makeQuery(id+"F1.opExtrude","CAP_FACE",FACE,{"disambiguationData":[OSD([sQuery(id+"F0.wireOp",EDGE,"E0.bottom"),sQuery(id+"F0.wireOp",EDGE,"E0.top"),subQ1,sQuery(id+"F0.wireOp",EDGE,"E0.right"),sQuery(id+"F0.wireOp",EDGE,"E1"),sQuery(id+"F0.wireOp",EDGE,"E2.0.1.0"),sQuery(id+"F0.wireOp",EDGE,"E2.0.2.0"),sQuery(id+"F0.wireOp",EDGE,"E2.0.3.0"),sQuery(id+"F0.wireOp",EDGE,"E2.0.4.0"),sQuery(id+"F0.wireOp",EDGE,"E2.0.5.0"),sQuery(id+"F0.wireOp",EDGE,"E2.1.0.0"),sQuery(id+"F0.wireOp",EDGE,"E2.1.1.0"),sQuery(id+"F0.wireOp",EDGE,"E2.1.2.0"),sQuery(id+"F0.wireOp",EDGE,"E2.1.3.0"),sQuery(id+"F0.wireOp",EDGE,"E2.1.4.0"),sQuery(id+"F0.wireOp",EDGE,"E2.1.5.0"),sQuery(id+"F0.wireOp",EDGE,"E3"),sQuery(id+"F0.wireOp",EDGE,"E4"),sQuery(id+"F0.wireOp",EDGE,"E5"),subQ0,sQuery(id+"F0.wireOp",EDGE,"E23"),sQuery(id+"F0.wireOp",EDGE,"E24"),sQuery(id+"F0.wireOp",EDGE,"E25"),sQuery(id+"F0.wireOp",EDGE,"E7.2"),sQuery(id+"F0.wireOp",EDGE,"E26"),sQuery(id+"F0.wireOp",EDGE,"E27"),sQuery(id+"F0.wireOp",EDGE,"E28.trimOffspring"),sQuery(id+"F0.wireOp",EDGE,"E29.trimOffspring"),sQuery(id+"F0.wireOp",EDGE,"E30.trimOffspring"),sQuery(id+"F0.wireOp",EDGE,"E31.trimOffspring"),sQuery(id+"F0.wireOp",EDGE,"E32.trimOffspring"),sQuery(id+"F0.wireOp",EDGE,"E33.trimOffspring"),sQuery(id+"F0.wireOp",EDGE,"E34.trimOffspring"),sQuery(id+"F0.wireOp",EDGE,"E18.trimOffspring"),sQuery(id+"F0.wireOp",EDGE,"E35"),sQuery(id+"F0.wireOp",EDGE,"E36.trimOffspring")])],"isStart":false})]});}
            var Q12;
            Q12=makeQuery(id+"F1.opExtrude","CAP_EDGE",EDGE,{"disambiguationData":[OSD([sQuery(id+"F0.wireOp",EDGE,"E0.left")])],"isStart":false});
            var Q13;
            {var subQ0=sQuery(id+"F0.wireOp",EDGE,"E3");var subQ1=sQuery(id+"F0.wireOp",EDGE,"E0.left");Q13=makeQuery(id+"F3.opFillet","BLEND_EDGE",EDGE,{"blendedFrom":[makeQuery(id+"F1.opExtrude","SWEPT_EDGE",EDGE,{"disambiguationData":[OSD([subQ1,subQ0])]}),makeQuery(id+"F1.opExtrude","CAP_FACE",FACE,{"disambiguationData":[OSD([sQuery(id+"F0.wireOp",EDGE,"E0.bottom"),sQuery(id+"F0.wireOp",EDGE,"E0.top"),subQ1,sQuery(id+"F0.wireOp",EDGE,"E0.right"),sQuery(id+"F0.wireOp",EDGE,"E1"),sQuery(id+"F0.wireOp",EDGE,"E2.0.1.0"),sQuery(id+"F0.wireOp",EDGE,"E2.0.2.0"),sQuery(id+"F0.wireOp",EDGE,"E2.0.3.0"),sQuery(id+"F0.wireOp",EDGE,"E2.0.4.0"),sQuery(id+"F0.wireOp",EDGE,"E2.0.5.0"),sQuery(id+"F0.wireOp",EDGE,"E2.1.0.0"),sQuery(id+"F0.wireOp",EDGE,"E2.1.1.0"),sQuery(id+"F0.wireOp",EDGE,"E2.1.2.0"),sQuery(id+"F0.wireOp",EDGE,"E2.1.3.0"),sQuery(id+"F0.wireOp",EDGE,"E2.1.4.0"),sQuery(id+"F0.wireOp",EDGE,"E2.1.5.0"),subQ0,sQuery(id+"F0.wireOp",EDGE,"E4"),sQuery(id+"F0.wireOp",EDGE,"E5"),sQuery(id+"F0.wireOp",EDGE,"E6"),sQuery(id+"F0.wireOp",EDGE,"E23"),sQuery(id+"F0.wireOp",EDGE,"E24"),sQuery(id+"F0.wireOp",EDGE,"E25"),sQuery(id+"F0.wireOp",EDGE,"E7.2"),sQuery(id+"F0.wireOp",EDGE,"E26"),sQuery(id+"F0.wireOp",EDGE,"E27"),sQuery(id+"F0.wireOp",EDGE,"E28.trimOffspring"),sQuery(id+"F0.wireOp",EDGE,"E29.trimOffspring"),sQuery(id+"F0.wireOp",EDGE,"E30.trimOffspring"),sQuery(id+"F0.wireOp",EDGE,"E31.trimOffspring"),sQuery(id+"F0.wireOp",EDGE,"E32.trimOffspring"),sQuery(id+"F0.wireOp",EDGE,"E33.trimOffspring"),sQuery(id+"F0.wireOp",EDGE,"E34.trimOffspring"),sQuery(id+"F0.wireOp",EDGE,"E18.trimOffspring"),sQuery(id+"F0.wireOp",EDGE,"E35"),sQuery(id+"F0.wireOp",EDGE,"E36.trimOffspring")])],"isStart":false})],"blendedInto":[makeQuery(id+"F1.opExtrude","CAP_FACE",FACE,{"disambiguationData":[OSD([sQuery(id+"F0.wireOp",EDGE,"E0.bottom"),sQuery(id+"F0.wireOp",EDGE,"E0.top"),subQ1,sQuery(id+"F0.wireOp",EDGE,"E0.right"),sQuery(id+"F0.wireOp",EDGE,"E1"),sQuery(id+"F0.wireOp",EDGE,"E2.0.1.0"),sQuery(id+"F0.wireOp",EDGE,"E2.0.2.0"),sQuery(id+"F0.wireOp",EDGE,"E2.0.3.0"),sQuery(id+"F0.wireOp",EDGE,"E2.0.4.0"),sQuery(id+"F0.wireOp",EDGE,"E2.0.5.0"),sQuery(id+"F0.wireOp",EDGE,"E2.1.0.0"),sQuery(id+"F0.wireOp",EDGE,"E2.1.1.0"),sQuery(id+"F0.wireOp",EDGE,"E2.1.2.0"),sQuery(id+"F0.wireOp",EDGE,"E2.1.3.0"),sQuery(id+"F0.wireOp",EDGE,"E2.1.4.0"),sQuery(id+"F0.wireOp",EDGE,"E2.1.5.0"),subQ0,sQuery(id+"F0.wireOp",EDGE,"E4"),sQuery(id+"F0.wireOp",EDGE,"E5"),sQuery(id+"F0.wireOp",EDGE,"E6"),sQuery(id+"F0.wireOp",EDGE,"E23"),sQuery(id+"F0.wireOp",EDGE,"E24"),sQuery(id+"F0.wireOp",EDGE,"E25"),sQuery(id+"F0.wireOp",EDGE,"E7.2"),sQuery(id+"F0.wireOp",EDGE,"E26"),sQuery(id+"F0.wireOp",EDGE,"E27"),sQuery(id+"F0.wireOp",EDGE,"E28.trimOffspring"),sQuery(id+"F0.wireOp",EDGE,"E29.trimOffspring"),sQuery(id+"F0.wireOp",EDGE,"E30.trimOffspring"),sQuery(id+"F0.wireOp",EDGE,"E31.trimOffspring"),sQuery(id+"F0.wireOp",EDGE,"E32.trimOffspring"),sQuery(id+"F0.wireOp",EDGE,"E33.trimOffspring"),sQuery(id+"F0.wireOp",EDGE,"E34.trimOffspring"),sQuery(id+"F0.wireOp",EDGE,"E18.trimOffspring"),sQuery(id+"F0.wireOp",EDGE,"E35"),sQuery(id+"F0.wireOp",EDGE,"E36.trimOffspring")])],"isStart":false})]});}
            var Q14;
            Q14=makeQuery(id+"F1.opExtrude","CAP_EDGE",EDGE,{"disambiguationData":[OSD([sQuery(id+"F0.wireOp",EDGE,"E3")])],"isStart":false});
            var Q15;
            {var subQ0=sQuery(id+"F0.wireOp",EDGE,"E3");var subQ1=sQuery(id+"F0.wireOp",EDGE,"E0.bottom");Q15=makeQuery(id+"F3.opFillet","BLEND_EDGE",EDGE,{"blendedFrom":[makeQuery(id+"F1.opExtrude","SWEPT_EDGE",EDGE,{"disambiguationData":[OSD([subQ1,subQ0])]}),makeQuery(id+"F1.opExtrude","CAP_FACE",FACE,{"disambiguationData":[OSD([subQ1,sQuery(id+"F0.wireOp",EDGE,"E0.top"),sQuery(id+"F0.wireOp",EDGE,"E0.left"),sQuery(id+"F0.wireOp",EDGE,"E0.right"),sQuery(id+"F0.wireOp",EDGE,"E1"),sQuery(id+"F0.wireOp",EDGE,"E2.0.1.0"),sQuery(id+"F0.wireOp",EDGE,"E2.0.2.0"),sQuery(id+"F0.wireOp",EDGE,"E2.0.3.0"),sQuery(id+"F0.wireOp",EDGE,"E2.0.4.0"),sQuery(id+"F0.wireOp",EDGE,"E2.0.5.0"),sQuery(id+"F0.wireOp",EDGE,"E2.1.0.0"),sQuery(id+"F0.wireOp",EDGE,"E2.1.1.0"),sQuery(id+"F0.wireOp",EDGE,"E2.1.2.0"),sQuery(id+"F0.wireOp",EDGE,"E2.1.3.0"),sQuery(id+"F0.wireOp",EDGE,"E2.1.4.0"),sQuery(id+"F0.wireOp",EDGE,"E2.1.5.0"),subQ0,sQuery(id+"F0.wireOp",EDGE,"E4"),sQuery(id+"F0.wireOp",EDGE,"E5"),sQuery(id+"F0.wireOp",EDGE,"E6"),sQuery(id+"F0.wireOp",EDGE,"E23"),sQuery(id+"F0.wireOp",EDGE,"E24"),sQuery(id+"F0.wireOp",EDGE,"E25"),sQuery(id+"F0.wireOp",EDGE,"E7.2"),sQuery(id+"F0.wireOp",EDGE,"E26"),sQuery(id+"F0.wireOp",EDGE,"E27"),sQuery(id+"F0.wireOp",EDGE,"E28.trimOffspring"),sQuery(id+"F0.wireOp",EDGE,"E29.trimOffspring"),sQuery(id+"F0.wireOp",EDGE,"E30.trimOffspring"),sQuery(id+"F0.wireOp",EDGE,"E31.trimOffspring"),sQuery(id+"F0.wireOp",EDGE,"E32.trimOffspring"),sQuery(id+"F0.wireOp",EDGE,"E33.trimOffspring"),sQuery(id+"F0.wireOp",EDGE,"E34.trimOffspring"),sQuery(id+"F0.wireOp",EDGE,"E18.trimOffspring"),sQuery(id+"F0.wireOp",EDGE,"E35"),sQuery(id+"F0.wireOp",EDGE,"E36.trimOffspring")])],"isStart":false})],"blendedInto":[makeQuery(id+"F1.opExtrude","CAP_FACE",FACE,{"disambiguationData":[OSD([subQ1,sQuery(id+"F0.wireOp",EDGE,"E0.top"),sQuery(id+"F0.wireOp",EDGE,"E0.left"),sQuery(id+"F0.wireOp",EDGE,"E0.right"),sQuery(id+"F0.wireOp",EDGE,"E1"),sQuery(id+"F0.wireOp",EDGE,"E2.0.1.0"),sQuery(id+"F0.wireOp",EDGE,"E2.0.2.0"),sQuery(id+"F0.wireOp",EDGE,"E2.0.3.0"),sQuery(id+"F0.wireOp",EDGE,"E2.0.4.0"),sQuery(id+"F0.wireOp",EDGE,"E2.0.5.0"),sQuery(id+"F0.wireOp",EDGE,"E2.1.0.0"),sQuery(id+"F0.wireOp",EDGE,"E2.1.1.0"),sQuery(id+"F0.wireOp",EDGE,"E2.1.2.0"),sQuery(id+"F0.wireOp",EDGE,"E2.1.3.0"),sQuery(id+"F0.wireOp",EDGE,"E2.1.4.0"),sQuery(id+"F0.wireOp",EDGE,"E2.1.5.0"),subQ0,sQuery(id+"F0.wireOp",EDGE,"E4"),sQuery(id+"F0.wireOp",EDGE,"E5"),sQuery(id+"F0.wireOp",EDGE,"E6"),sQuery(id+"F0.wireOp",EDGE,"E23"),sQuery(id+"F0.wireOp",EDGE,"E24"),sQuery(id+"F0.wireOp",EDGE,"E25"),sQuery(id+"F0.wireOp",EDGE,"E7.2"),sQuery(id+"F0.wireOp",EDGE,"E26"),sQuery(id+"F0.wireOp",EDGE,"E27"),sQuery(id+"F0.wireOp",EDGE,"E28.trimOffspring"),sQuery(id+"F0.wireOp",EDGE,"E29.trimOffspring"),sQuery(id+"F0.wireOp",EDGE,"E30.trimOffspring"),sQuery(id+"F0.wireOp",EDGE,"E31.trimOffspring"),sQuery(id+"F0.wireOp",EDGE,"E32.trimOffspring"),sQuery(id+"F0.wireOp",EDGE,"E33.trimOffspring"),sQuery(id+"F0.wireOp",EDGE,"E34.trimOffspring"),sQuery(id+"F0.wireOp",EDGE,"E18.trimOffspring"),sQuery(id+"F0.wireOp",EDGE,"E35"),sQuery(id+"F0.wireOp",EDGE,"E36.trimOffspring")])],"isStart":false})]});}
            var Q16;
            Q16=makeQuery(id+"F1.opExtrude","CAP_EDGE",EDGE,{"disambiguationData":[OSD([sQuery(id+"F0.wireOp",EDGE,"E30.trimOffspring")])],"isStart":false});
            var Q17;
            Q17=makeQuery(id+"F1.opExtrude","CAP_EDGE",EDGE,{"disambiguationData":[OSD([sQuery(id+"F0.wireOp",EDGE,"E34.trimOffspring")])],"isStart":false});
            var Q18;
            Q18=makeQuery(id+"F1.opExtrude","CAP_EDGE",EDGE,{"disambiguationData":[OSD([sQuery(id+"F0.wireOp",EDGE,"E29.trimOffspring")])],"isStart":false});
            var Q19;
            Q19=makeQuery(id+"F1.opExtrude","CAP_EDGE",EDGE,{"disambiguationData":[OSD([sQuery(id+"F0.wireOp",EDGE,"E25")])],"isStart":false});
            var Q20;
            Q20=makeQuery(id+"F1.opExtrude","CAP_EDGE",EDGE,{"disambiguationData":[OSD([sQuery(id+"F0.wireOp",EDGE,"E24")])],"isStart":false});
            var Q21;
            Q21=makeQuery(id+"F1.opExtrude","CAP_EDGE",EDGE,{"disambiguationData":[OSD([sQuery(id+"F0.wireOp",EDGE,"E27")])],"isStart":false});
            var Q22;
            Q22=makeQuery(id+"F1.opExtrude","CAP_EDGE",EDGE,{"disambiguationData":[OSD([sQuery(id+"F0.wireOp",EDGE,"E28.trimOffspring")])],"isStart":false});
            var Q23;
            Q23=makeQuery(id+"F1.opExtrude","CAP_EDGE",EDGE,{"disambiguationData":[OSD([sQuery(id+"F0.wireOp",EDGE,"E31.trimOffspring")])],"isStart":false});
            var Q24;
            Q24=makeQuery(id+"F1.opExtrude","CAP_EDGE",EDGE,{"disambiguationData":[OSD([sQuery(id+"F0.wireOp",EDGE,"E33.trimOffspring")])],"isStart":false});
            var Q25;
            Q25=makeQuery(id+"F1.opExtrude","CAP_EDGE",EDGE,{"disambiguationData":[OSD([sQuery(id+"F0.wireOp",EDGE,"E36.trimOffspring")])],"isStart":false});
            var Q26;
            Q26=makeQuery(id+"F1.opExtrude","CAP_EDGE",EDGE,{"disambiguationData":[OSD([sQuery(id+"F0.wireOp",EDGE,"E23")])],"isStart":false});
            var Q27;
            Q27=makeQuery(id+"F1.opExtrude","CAP_EDGE",EDGE,{"disambiguationData":[OSD([sQuery(id+"F0.wireOp",EDGE,"E35")])],"isStart":false});
            var Q28;
            Q28=makeQuery(id+"F1.opExtrude","CAP_EDGE",EDGE,{"disambiguationData":[OSD([sQuery(id+"F0.wireOp",EDGE,"E32.trimOffspring")])],"isStart":false});
            var Q29;
            Q29=makeQuery(id+"F1.opExtrude","CAP_EDGE",EDGE,{"disambiguationData":[OSD([sQuery(id+"F0.wireOp",EDGE,"E7.2")])],"isStart":false});
            var Q30;
            Q30=makeQuery(id+"F1.opExtrude","CAP_EDGE",EDGE,{"disambiguationData":[OSD([sQuery(id+"F0.wireOp",EDGE,"E18.trimOffspring")])],"isStart":false});
            var Q31;
            Q31=makeQuery(id+"F1.opExtrude","CAP_EDGE",EDGE,{"disambiguationData":[OSD([sQuery(id+"F0.wireOp",EDGE,"E26")])],"isStart":false});
            fillet(context, id + "F5", {"entities" : qUnion([Q0, Q1, Q2, Q3, Q4, Q5, Q6, Q7, Q8, Q9, Q10, Q11, Q12, Q13, Q14, Q15, Q16, Q17, Q18, Q19, Q20, Q21, Q22, Q23, Q24, Q25, Q26, Q27, Q28, Q29, Q30, Q31]), "radius" : 1 * mm, "tangentPropagation" : true, "allowEdgeOverflow" : false});
        }
    });
